# Revit family: Double Width Outline Units
name_source: partatom
category: Furniture
units: mm (PartAtom-declared; Revit-internal decimal feet)

## family parameters
Always vertical = Yes
Cut with Voids When Loaded = No
OmniClass Number = 23.40.20.00
OmniClass Title = General Furniture and Specialties
Room Calculation Point = No
Shared = No
Work Plane-Based = No

## types (16) — shared parameters
AssetType = Fixed
Category = PR_40_30_78_57
Color = Vision Pallete
DurationUnit = Years
ExpectedLife = 10
Finish = Powder Coated Steel
Keynote = PR_40_30_78_57
ManufacturerName = Bisley
ManufacturerURL = www.bisley.com
Material = Steel
Model = Outline
NBSDescription = Office storage
NBSReference = 45-35-80/360
Name = Floor Standing Outline Frames
ProductInformation = https://www.bisley.com
Revision = 1
Shape = Rectangular
Uniclass2015Code = PR_40_30_78_57
Uniclass2015Title = 78 - Shelves and Storage Units
Uniclass2015Version = V1.1
WarrantyDescription = Standard Bisley Warranty
WarrantyDurationUnit = Year
zero-valued in all types: Default Elevation

## per-type parameters (varying)
| type | Depth | Frame Type | Height | ModelNumber | ModelReference | NominalHeight | NominalLength | NominalWidth | Plinth Height | Shelf Type | Width |
| OF08402 | 400 mm  [stored 1.31234 ft] | Outline Frames : 800w 2 High | 753 mm  [stored 2.47047 ft] | OF08402 | OF08402 | 753 mm  [stored 2.47047 ft] | 400 mm  [stored 1.31234 ft] | 800 mm  [stored 2.62467 ft] | 50 mm  [stored 0.164042 ft] | Shelves : Steel Shelf 800w units | 800 mm  [stored 2.62467 ft] |
| OF10402 | 400 mm  [stored 1.31234 ft] | Outline Frames : 1000w 2 High | 753 mm  [stored 2.47047 ft] | OF10402 | OF10402 | 753 mm  [stored 2.47047 ft] | 400 mm  [stored 1.31234 ft] | 1000 mm  [stored 3.28084 ft] | 50 mm  [stored 0.164042 ft] | Shelves : Steel Shelf 1000w units | 1000 mm  [stored 3.28084 ft] |
| OF08472 | 470 mm  [stored 1.54199 ft] | Outline Frames : 800w 2 High 470d | 812 mm  [stored 2.66404 ft] | OF08472 | OF08472 | 812 mm  [stored 2.66404 ft] | 470 mm  [stored 1.54199 ft] | 800 mm  [stored 2.62467 ft] | 40 mm  [stored 0.131234 ft] | Shelves : Steel Shelf 800w units 470d | 800 mm  [stored 2.62467 ft] |
| OF10472 | 470 mm  [stored 1.54199 ft] | Outline Frames : 1000w 2 High 470d | 812 mm  [stored 2.66404 ft] | OF10472 | OF10472 | 812 mm  [stored 2.66404 ft] | 470 mm  [stored 1.54199 ft] | 1000 mm  [stored 3.28084 ft] | 40 mm  [stored 0.131234 ft] | Shelves : Steel Shelf 1000w units 470 deep | 1000 mm  [stored 3.28084 ft] |
| OF08403 | 400 mm  [stored 1.31234 ft] | Outline Frames : 800w 3 High | 1133 mm  [stored 3.71719 ft] | OF08403 | OF08403 | 1133 mm  [stored 3.71719 ft] | 400 mm  [stored 1.31234 ft] | 800 mm  [stored 2.62467 ft] | 50 mm  [stored 0.164042 ft] | Shelves : Steel Shelf 800w units | 800 mm  [stored 2.62467 ft] |
| OF10403 | 400 mm  [stored 1.31234 ft] | Outline Frames : 1000w 3 High | 1133 mm  [stored 3.71719 ft] | OF10403 | OF10403 | 1133 mm  [stored 3.71719 ft] | 400 mm  [stored 1.31234 ft] | 1000 mm  [stored 3.28084 ft] | 50 mm  [stored 0.164042 ft] | Shelves : Steel Shelf 1000w units | 1000 mm  [stored 3.28084 ft] |
| OF08473 | 470 mm  [stored 1.54199 ft] | Outline Frames : 800w 3 High 470d | 1199 mm  [stored 3.93373 ft] | OF08473 | OF08473 | 1199 mm  [stored 3.93373 ft] | 470 mm  [stored 1.54199 ft] | 800 mm  [stored 2.62467 ft] | 40 mm  [stored 0.131234 ft] | Shelves : Steel Shelf 800w units 470d | 800 mm  [stored 2.62467 ft] |
| OF10473 | 470 mm  [stored 1.54199 ft] | Outline Frames : 1000w 3 High 470d | 1199 mm  [stored 3.93373 ft] | OF10473 | OF10473 | 1199 mm  [stored 3.93373 ft] | 470 mm  [stored 1.54199 ft] | 1000 mm  [stored 3.28084 ft] | 40 mm  [stored 0.131234 ft] | Shelves : Steel Shelf 1000w units 470 deep | 1000 mm  [stored 3.28084 ft] |
| OF08404 | 400 mm  [stored 1.31234 ft] | Outline Frames : 800w 4 High | 1512 mm  [stored 4.96063 ft] | OF08404 | OF08404 | 1512 mm  [stored 4.96063 ft] | 400 mm  [stored 1.31234 ft] | 800 mm  [stored 2.62467 ft] | 50 mm  [stored 0.164042 ft] | Shelves : Steel Shelf 800w units | 800 mm  [stored 2.62467 ft] |
| OF10404 | 400 mm  [stored 1.31234 ft] | Outline Frames : 1000w 4 High | 1512 mm  [stored 4.96063 ft] | OF10404 | OF10404 | 1512 mm  [stored 4.96063 ft] | 400 mm  [stored 1.31234 ft] | 1000 mm  [stored 3.28084 ft] | 50 mm  [stored 0.164042 ft] | Shelves : Steel Shelf 1000w units | 1000 mm  [stored 3.28084 ft] |
| OF08474 | 470 mm  [stored 1.54199 ft] | Outline Frames : 800w 4 High 470d | 1585 mm  [stored 5.20013 ft] | OF08474 | OF08474 | 1585 mm  [stored 5.20013 ft] | 470 mm  [stored 1.54199 ft] | 800 mm  [stored 2.62467 ft] | 40 mm  [stored 0.131234 ft] | Shelves : Steel Shelf 800w units 470d | 800 mm  [stored 2.62467 ft] |
| OF10474 | 470 mm  [stored 1.54199 ft] | Outline Frames : 1000w 4 High 470d | 1585 mm  [stored 5.20013 ft] | OF10474 | OF10474 | 1585 mm  [stored 5.20013 ft] | 470 mm  [stored 1.54199 ft] | 1000 mm  [stored 3.28084 ft] | 40 mm  [stored 0.131234 ft] | Shelves : Steel Shelf 1000w units 470 deep | 1000 mm  [stored 3.28084 ft] |
| OF08405 | 400 mm  [stored 1.31234 ft] | Outline Frames : 800w 5 High | 1891 mm  [stored 6.20407 ft] | OF08405 | OF08405 | 1891 mm  [stored 6.20407 ft] | 400 mm  [stored 1.31234 ft] | 800 mm  [stored 2.62467 ft] | 50 mm  [stored 0.164042 ft] | Shelves : Steel Shelf 800w units | 800 mm  [stored 2.62467 ft] |
| OF10405 | 400 mm  [stored 1.31234 ft] | Outline Frames : 1000w 5 High | 1891 mm  [stored 6.20407 ft] | OF10405 | OF10405 | 1891 mm  [stored 6.20407 ft] | 400 mm  [stored 1.31234 ft] | 1000 mm  [stored 3.28084 ft] | 50 mm  [stored 0.164042 ft] | Shelves : Steel Shelf 1000w units | 1000 mm  [stored 3.28084 ft] |
| OF08475 | 470 mm  [stored 1.54199 ft] | Outline Frames : 800w 5 High 470d | 1968 mm  [stored 6.45669 ft] | OFO8475 | OFO8475 | 1968 mm  [stored 6.45669 ft] | 470 mm  [stored 1.54199 ft] | 800 mm  [stored 2.62467 ft] | 40 mm  [stored 0.131234 ft] | Shelves : Steel Shelf 800w units 470d | 800 mm  [stored 2.62467 ft] |
| OF10475 | 470 mm  [stored 1.54199 ft] | Outline Frames : 1000w 5 High 470d | 1968 mm  [stored 6.45669 ft] | OF10475 | OF10475 | 1968 mm  [stored 6.45669 ft] | 470 mm  [stored 1.54199 ft] | 1000 mm  [stored 3.28084 ft] | 40 mm  [stored 0.131234 ft] | Shelves : MFC Shelf 1000w units 470d | 1000 mm  [stored 3.28084 ft] |

note: [stored X ft] marks values corroborated as IEEE doubles in the binary element streams (Revit-internal decimal feet)

## geometry (parser evidence)
native form markers: Sweep x6
no freeform markers — native parametric forms only
